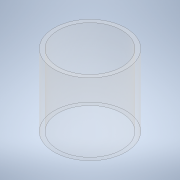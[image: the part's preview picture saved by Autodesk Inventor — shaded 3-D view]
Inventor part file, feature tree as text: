
AUTODESK INVENTOR PART (.ipt)
format: ipt  version: 2020 (Build 240168000, 168)  size: 115,712 bytes
history: native  units: mm
features: other x1, extrude x1, sketch x1
ambient origin geometry x8: Origin, YZ Plane, XZ Plane, XY Plane, X Axis, Y Axis, Z Axis, Center Point
bodies: Body1 (feature_tree)
feature tree (3):
  other  "Твердое тело1"
  extrude  "Выдавливание1"  Depth=50.0mm
  sketch  "Эскиз1"
